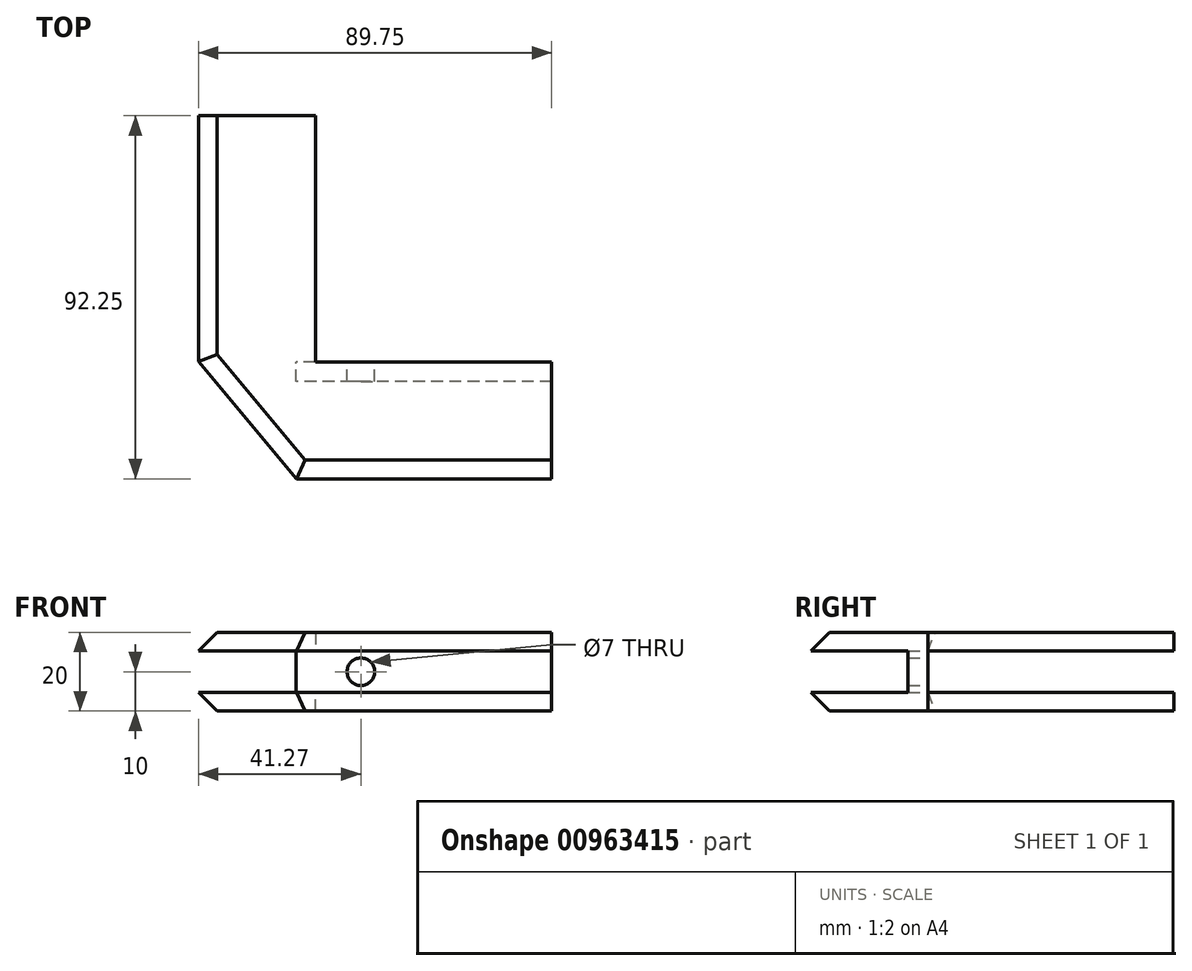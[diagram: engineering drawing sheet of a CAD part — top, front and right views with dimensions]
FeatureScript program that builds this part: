
annotation { "Feature Type Name" : "Feature", "Feature Type Description" : "" }
export const myFeature = defineFeature(function(context is Context, id is Id, definition is map)
    precondition{}
    {
        {
            var Q0;
            Q0=qCreatedBy(makeId("Top.planeOp"),FACE);
            var sketch = newSketch(context, id + "F0", { "sketchPlane" : qUnion([Q0])});
            skLineSegment(sketch, "E0.bottom", {"start": v(2.5, -2.5) * mm, "end": v(-2.5, -2.5) * mm});
            skLineSegment(sketch, "E0.top", {"start": v(2.5, 2.5) * mm, "end": v(-2.5, 2.5) * mm});
            skLineSegment(sketch, "E0.left", {"start": v(2.5, -2.5) * mm, "end": v(2.5, 2.5) * mm});
            skLineSegment(sketch, "E0.right", {"start": v(-2.5, -2.5) * mm, "end": v(-2.5, 2.5) * mm});
            skPoint(sketch, "E0.middle", {"position": v(0, 0) * mm});
            skLineSegment(sketch, "E1.bottom", {"start": v(2.5, 2.5) * mm, "end": v(62.5, 2.5) * mm});
            skLineSegment(sketch, "E1.top", {"start": v(2.5, -2.5) * mm, "end": v(62.5, -2.5) * mm});
            skLineSegment(sketch, "E1.left", {"start": v(2.5, 2.5) * mm, "end": v(2.5, -2.5) * mm});
            skLineSegment(sketch, "E1.right", {"start": v(62.5, 2.5) * mm, "end": v(62.5, -2.5) * mm});
            skLineSegment(sketch, "E2.bottom", {"start": v(-2.5, 2.5) * mm, "end": v(2.5, 2.5) * mm});
            skLineSegment(sketch, "E2.top", {"start": v(-2.5, 65) * mm, "end": v(2.5, 65) * mm});
            skLineSegment(sketch, "E2.left", {"start": v(-2.5, 2.5) * mm, "end": v(-2.5, 65) * mm});
            skLineSegment(sketch, "E2.right", {"start": v(2.5, 2.5) * mm, "end": v(2.5, 65) * mm});
            skSolve(sketch);
        }
        {
            var Q0;
            Q0=makeQuery(id+"F0.imprint","IMPRINT",FACE,{"disambiguationData":[TD([[makeQuery(id+"F0.imprint","IMPRINT",EDGE,{"derivedFrom":sQuery(id+"F0.wireOp",EDGE,"E2.bottom")}),1.0]])]});
            var Q1;
            Q1=makeQuery(id+"F0.imprint","IMPRINT",FACE,{"disambiguationData":[TD([[makeQuery(id+"F0.imprint","IMPRINT",EDGE,{"derivedFrom":sQuery(id+"F0.wireOp",EDGE,"E0.bottom")}),-1.0]])]});
            var Q2;
            Q2=makeQuery(id+"F0.imprint","IMPRINT",FACE,{"disambiguationData":[TD([[makeQuery(id+"F0.imprint","IMPRINT",EDGE,{"derivedFrom":sQuery(id+"F0.wireOp",EDGE,"E1.bottom")}),-1.0]])]});
            extrude(context, id + "F1", {"entities" : qUnion([Q0, Q1, Q2]), "depth" : 10.5 * mm, "offsetDistance" : 25 * mm});
        }
        {
            var Q0;
            Q0=makeQuery(id+"F1.opExtrude","CAP_FACE",FACE,{"disambiguationData":[OSD([sQuery(id+"F0.wireOp",EDGE,"E0.bottom"),sQuery(id+"F0.wireOp",EDGE,"E0.right"),sQuery(id+"F0.wireOp",EDGE,"E1.bottom"),sQuery(id+"F0.wireOp",EDGE,"E1.top"),sQuery(id+"F0.wireOp",EDGE,"E1.right"),sQuery(id+"F0.wireOp",EDGE,"E2.top"),sQuery(id+"F0.wireOp",EDGE,"E2.left"),sQuery(id+"F0.wireOp",EDGE,"E2.right")])],"isStart":false});
            var sketch = newSketch(context, id + "F2", { "sketchPlane" : qUnion([Q0])});
            skLineSegment(sketch, "E3.bottom", {"start": v(-2.5, 2.5) * mm, "end": v(62.5, 2.5) * mm});
            skLineSegment(sketch, "E3.top", {"start": v(-2.5, -27.5) * mm, "end": v(62.5, -27.5) * mm});
            skLineSegment(sketch, "E3.left", {"start": v(-2.5, 2.5) * mm, "end": v(-2.5, -27.5) * mm});
            skLineSegment(sketch, "E3.right", {"start": v(62.5, 2.5) * mm, "end": v(62.5, -27.5) * mm});
            skLineSegment(sketch, "E4.bottom", {"start": v(2.5, 65) * mm, "end": v(-27.5, 65) * mm});
            skLineSegment(sketch, "E4.top", {"start": v(2.5, 2.5) * mm, "end": v(-27.5, 2.5) * mm});
            skLineSegment(sketch, "E4.left", {"start": v(2.5, 65) * mm, "end": v(2.5, 2.5) * mm});
            skLineSegment(sketch, "E4.right", {"start": v(-27.5, 65) * mm, "end": v(-27.5, 2.5) * mm});
            skLineSegment(sketch, "E5", {"start": v(-27.5, 2.5) * mm, "end": v(-2.5, -27.5) * mm});
            skSolve(sketch);
        }
        {
            var Q0;
            {var subQ3=sQuery(id+"F2.wireOp",EDGE,"E4.left");Q0=makeQuery(id+"F2.imprint","IMPRINT",FACE,{"disambiguationData":[TD([[makeQuery(id+"F2.imprint","IMPRINT",EDGE,{"derivedFrom":subQ3}),1.0]])]});}
            var Q1;
            {var subQ3=sQuery(id+"F2.wireOp",EDGE,"E4.right");Q1=makeQuery(id+"F2.imprint","IMPRINT",FACE,{"disambiguationData":[TD([[makeQuery(id+"F2.imprint","IMPRINT",EDGE,{"derivedFrom":subQ3}),1.0]])]});}
            var Q2;
            {var subQ4=sQuery(id+"F2.wireOp",EDGE,"E5");Q2=makeQuery(id+"F2.imprint","IMPRINT",FACE,{"disambiguationData":[TD([[makeQuery(id+"F2.imprint","IMPRINT",EDGE,{"derivedFrom":subQ4}),1.0]])]});}
            var Q3;
            {var subQ0=sQuery(id+"F2.wireOp",EDGE,"E3.top");Q3=makeQuery(id+"F2.imprint","IMPRINT",FACE,{"disambiguationData":[TD([[makeQuery(id+"F2.imprint","IMPRINT",EDGE,{"derivedFrom":subQ0}),1.0]])]});}
            var Q4;
            {var subQ5=makeQuery(id+"F1.opExtrude","CAP_EDGE",EDGE,{"disambiguationData":[OSD([sQuery(id+"F0.wireOp",EDGE,"E0.bottom"),sQuery(id+"F0.wireOp",EDGE,"E1.top")])],"isStart":false});Q4=makeQuery(id+"F2.imprint","IMPRINT",FACE,{"disambiguationData":[TD([[makeQuery(id+"F2.imprint","IMPRINT",EDGE,{"derivedFrom":subQ5}),-1.0]])]});}
            extrude(context, id + "F3", {"entities" : qUnion([Q0, Q1, Q2, Q3, Q4]), "operationType" : NewBodyOperationType.ADD, "depth" : 4.75 * mm, "offsetDistance" : 25 * mm});
        }
        {
            var Q0;
            Q0=makeQuery(id+"F1.opExtrude","CAP_FACE",FACE,{"disambiguationData":[OSD([sQuery(id+"F0.wireOp",EDGE,"E0.bottom"),sQuery(id+"F0.wireOp",EDGE,"E0.right"),sQuery(id+"F0.wireOp",EDGE,"E1.bottom"),sQuery(id+"F0.wireOp",EDGE,"E1.top"),sQuery(id+"F0.wireOp",EDGE,"E1.right"),sQuery(id+"F0.wireOp",EDGE,"E2.top"),sQuery(id+"F0.wireOp",EDGE,"E2.left"),sQuery(id+"F0.wireOp",EDGE,"E2.right")])],"isStart":true});
            var sketch = newSketch(context, id + "F4", { "sketchPlane" : qUnion([Q0])});
            skLineSegment(sketch, "E6.bottom", {"start": v(62.5, -2.5) * mm, "end": v(-2.5, -2.5) * mm});
            skLineSegment(sketch, "E6.top", {"start": v(62.5, 27.5) * mm, "end": v(-2.5, 27.5) * mm});
            skLineSegment(sketch, "E6.left", {"start": v(62.5, -2.5) * mm, "end": v(62.5, 27.5) * mm});
            skLineSegment(sketch, "E6.right", {"start": v(-2.5, -2.5) * mm, "end": v(-2.5, 27.5) * mm});
            skLineSegment(sketch, "E7.bottom", {"start": v(2.5, -65) * mm, "end": v(-27.5, -65) * mm});
            skLineSegment(sketch, "E7.top", {"start": v(2.5, -2.5) * mm, "end": v(-27.5, -2.5) * mm});
            skLineSegment(sketch, "E7.left", {"start": v(2.5, -65) * mm, "end": v(2.5, -2.5) * mm});
            skLineSegment(sketch, "E7.right", {"start": v(-27.5, -65) * mm, "end": v(-27.5, -2.5) * mm});
            skLineSegment(sketch, "E8", {"start": v(-27.5, -2.5) * mm, "end": v(-2.5, 27.5) * mm});
            skSolve(sketch);
        }
        {
            var Q0;
            {var subQ0=sQuery(id+"F4.wireOp",EDGE,"E6.top");Q0=makeQuery(id+"F4.imprint","IMPRINT",FACE,{"disambiguationData":[TD([[makeQuery(id+"F4.imprint","IMPRINT",EDGE,{"derivedFrom":subQ0}),1.0]])]});}
            var Q1;
            {var subQ1=makeQuery(id+"F1.opExtrude","CAP_EDGE",EDGE,{"disambiguationData":[OSD([sQuery(id+"F0.wireOp",EDGE,"E0.bottom"),sQuery(id+"F0.wireOp",EDGE,"E1.top")])],"isStart":true});Q1=makeQuery(id+"F4.imprint","IMPRINT",FACE,{"disambiguationData":[TD([[makeQuery(id+"F4.imprint","IMPRINT",EDGE,{"derivedFrom":subQ1}),1.0]])]});}
            var Q2;
            {var subQ4=sQuery(id+"F4.wireOp",EDGE,"E8");Q2=makeQuery(id+"F4.imprint","IMPRINT",FACE,{"disambiguationData":[TD([[makeQuery(id+"F4.imprint","IMPRINT",EDGE,{"derivedFrom":subQ4}),-1.0]])]});}
            var Q3;
            {var subQ3=sQuery(id+"F4.wireOp",EDGE,"E7.left");Q3=makeQuery(id+"F4.imprint","IMPRINT",FACE,{"disambiguationData":[TD([[makeQuery(id+"F4.imprint","IMPRINT",EDGE,{"derivedFrom":subQ3}),-1.0]])]});}
            var Q4;
            {var subQ3=sQuery(id+"F4.wireOp",EDGE,"E7.right");Q4=makeQuery(id+"F4.imprint","IMPRINT",FACE,{"disambiguationData":[TD([[makeQuery(id+"F4.imprint","IMPRINT",EDGE,{"derivedFrom":subQ3}),-1.0]])]});}
            extrude(context, id + "F5", {"entities" : qUnion([Q0, Q1, Q2, Q3, Q4]), "operationType" : NewBodyOperationType.ADD, "depth" : 4.75 * mm, "offsetDistance" : 25 * mm});
        }
        {
            var Q0;
            Q0=makeQuery(id+"F3.opExtrude","CAP_EDGE",EDGE,{"disambiguationData":[OSD([sQuery(id+"F2.wireOp",EDGE,"E4.right")])],"isStart":false});
            chamfer(context, id + "F6", {"entities" : qUnion([Q0]), "width" : 5 * mm, "tangentPropagation" : true});
        }
        {
            var Q0;
            Q0=makeQuery(id+"F3.opExtrude","CAP_EDGE",EDGE,{"disambiguationData":[OSD([sQuery(id+"F2.wireOp",EDGE,"E5")])],"isStart":false});
            var Q1;
            Q1=makeQuery(id+"F3.opExtrude","CAP_EDGE",EDGE,{"disambiguationData":[OSD([sQuery(id+"F2.wireOp",EDGE,"E3.top")])],"isStart":false});
            var Q2;
            Q2=makeQuery(id+"F5.opExtrude","CAP_EDGE",EDGE,{"disambiguationData":[OSD([sQuery(id+"F4.wireOp",EDGE,"E7.right")])],"isStart":false});
            var Q3;
            Q3=makeQuery(id+"F5.opExtrude","CAP_EDGE",EDGE,{"disambiguationData":[OSD([sQuery(id+"F4.wireOp",EDGE,"E8")])],"isStart":false});
            var Q4;
            Q4=makeQuery(id+"F5.opExtrude","CAP_EDGE",EDGE,{"disambiguationData":[OSD([sQuery(id+"F4.wireOp",EDGE,"E6.top")])],"isStart":false});
            chamfer(context, id + "F7", {"entities" : qUnion([Q0, Q1, Q2, Q3, Q4]), "width" : 5 * mm, "tangentPropagation" : true});
        }
        {
            var Q0;
            Q0=makeQuery(id+"F5.boolean.opBoolean","MERGE",FACE,{"derivedFrom":[makeQuery(id+"F3.boolean.opBoolean","MERGE",FACE,{"derivedFrom":[makeQuery(id+"F1.opExtrude","SWEPT_FACE",FACE,{"disambiguationData":[OSD([sQuery(id+"F0.wireOp",EDGE,"E1.bottom")])]}),makeQuery(id+"F3.opExtrude","SWEPT_FACE",FACE,{"disambiguationData":[OSD([sQuery(id+"F2.wireOp",EDGE,"E3.bottom")])]})]}),makeQuery(id+"F5.opExtrude","SWEPT_FACE",FACE,{"disambiguationData":[OSD([sQuery(id+"F4.wireOp",EDGE,"E6.bottom")])]})]});
            var sketch = newSketch(context, id + "F8", { "sketchPlane" : qUnion([Q0])});
            skLineSegment(sketch, "E9", {"start": v(-62.5, 5.25) * mm, "end": v(-2.5, 5.25) * mm, "construction": true});
            skPoint(sketch, "E10", {"position": v(-14.02, 5.25) * mm});
            skSolve(sketch);
        }
        {
            var Q0;
            Q0=sQuery(id+"F8.wireOp",VERTEX,"E10");
            var Q1;
            Q1=makeQuery(id+"F1.opExtrude","SWEPT_BODY",BODY,{"disambiguationData":[OSD([sQuery(id+"F0.wireOp",EDGE,"E0.bottom"),sQuery(id+"F0.wireOp",EDGE,"E0.right"),sQuery(id+"F0.wireOp",EDGE,"E1.bottom"),sQuery(id+"F0.wireOp",EDGE,"E1.top"),sQuery(id+"F0.wireOp",EDGE,"E1.right"),sQuery(id+"F0.wireOp",EDGE,"E2.top"),sQuery(id+"F0.wireOp",EDGE,"E2.left"),sQuery(id+"F0.wireOp",EDGE,"E2.right")])]});
            hole(context, id + "F9", {"style" : HoleStyle.SIMPLE, "endStyle" : HoleEndStyle.THROUGH, "holeDiameter" : 7 * mm, "majorDiameter" : 5 * mm, "isTappedThrough" : true, "tappedDepth" : 12 * mm, "tapClearance" : 3, "locations" : qUnion([Q0]), "scope" : qUnion([Q1])});
        }
    });
